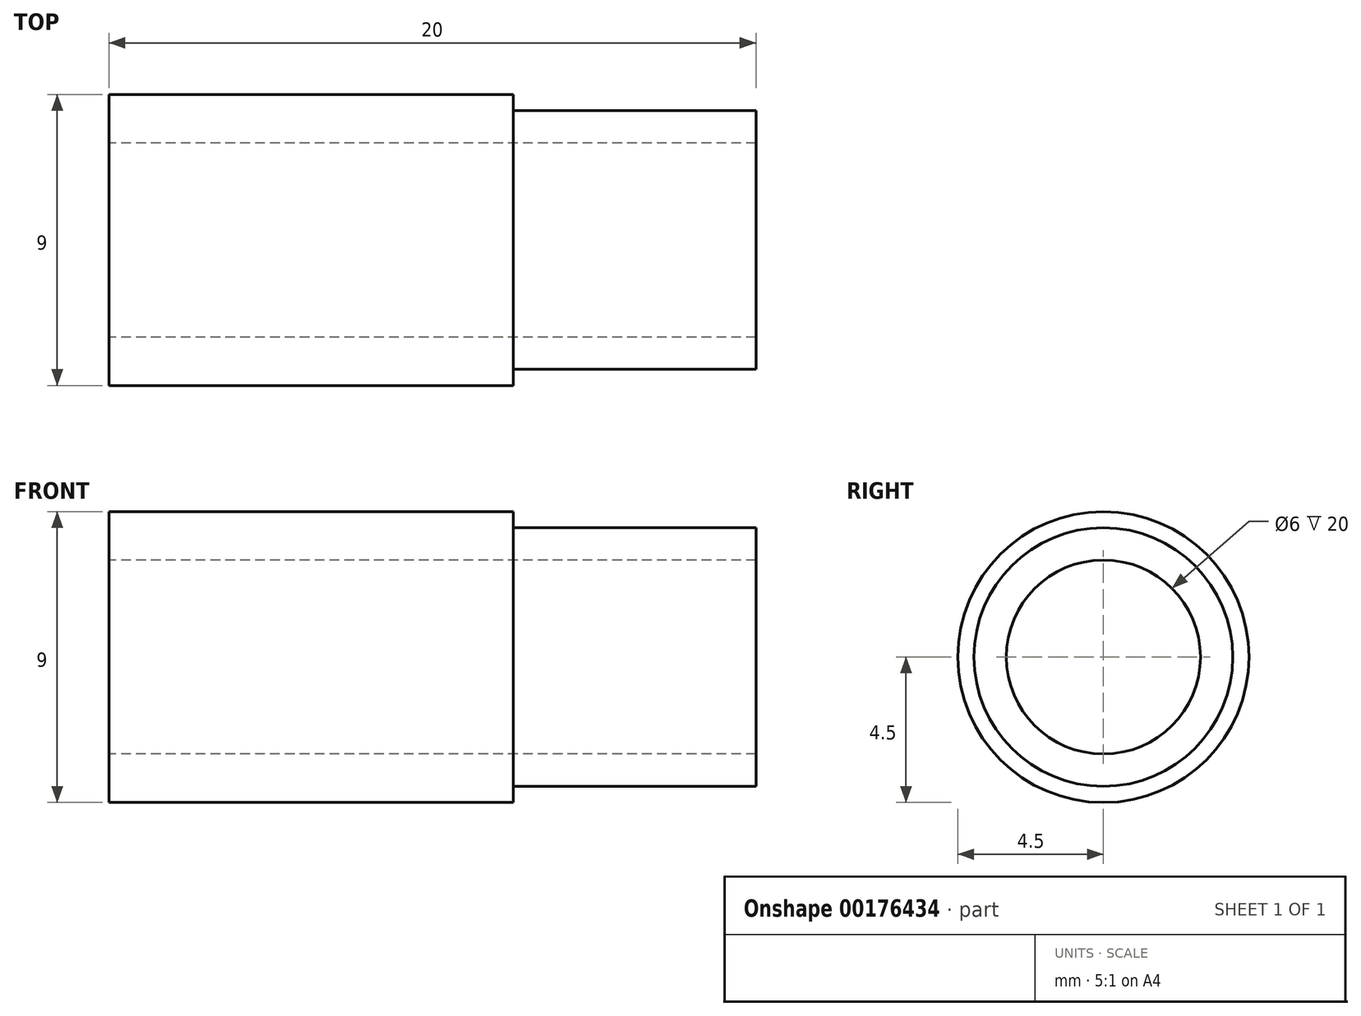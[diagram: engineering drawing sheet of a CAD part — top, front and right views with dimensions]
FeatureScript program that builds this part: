
annotation { "Feature Type Name" : "Feature", "Feature Type Description" : "" }
export const myFeature = defineFeature(function(context is Context, id is Id, definition is map)
    precondition{}
    {
        {
            var Q0;
            Q0=qCreatedBy(makeId("Right.planeOp"),FACE);
            var sketch = newSketch(context, id + "F0", { "sketchPlane" : qUnion([Q0])});
            skCircle(sketch, "E0", {"center": v(0, 0) * mm, "radius": 3 * mm});
            skCircle(sketch, "E1", {"center": v(0, 0) * mm, "radius": 4 * mm});
            skCircle(sketch, "E2", {"center": v(0, 0) * mm, "radius": 4.5 * mm});
            skSolve(sketch);
        }
        {
            var Q0;
            Q0=makeQuery(id+"F0.imprint","IMPRINT",FACE,{"disambiguationData":[TD([[makeQuery(id+"F0.imprint","IMPRINT",EDGE,{"derivedFrom":sQuery(id+"F0.wireOp",EDGE,"E0")}),-1.0]])]});
            extrude(context, id + "F1", {"entities" : qUnion([Q0]), "depth" : 7.5 * mm, "hasSecondDirection" : true, "secondDirectionOppositeDirection" : true, "secondDirectionDepth" : 12.5 * mm});
        }
        {
            var Q0;
            Q0=makeQuery(id+"F0.imprint","IMPRINT",FACE,{"disambiguationData":[TD([[makeQuery(id+"F0.imprint","IMPRINT",EDGE,{"derivedFrom":sQuery(id+"F0.wireOp",EDGE,"E1")}),-1.0]])]});
            extrude(context, id + "F2", {"entities" : qUnion([Q0]), "operationType" : NewBodyOperationType.ADD, "oppositeDirection" : true, "depth" : 12.5 * mm});
        }
    });
